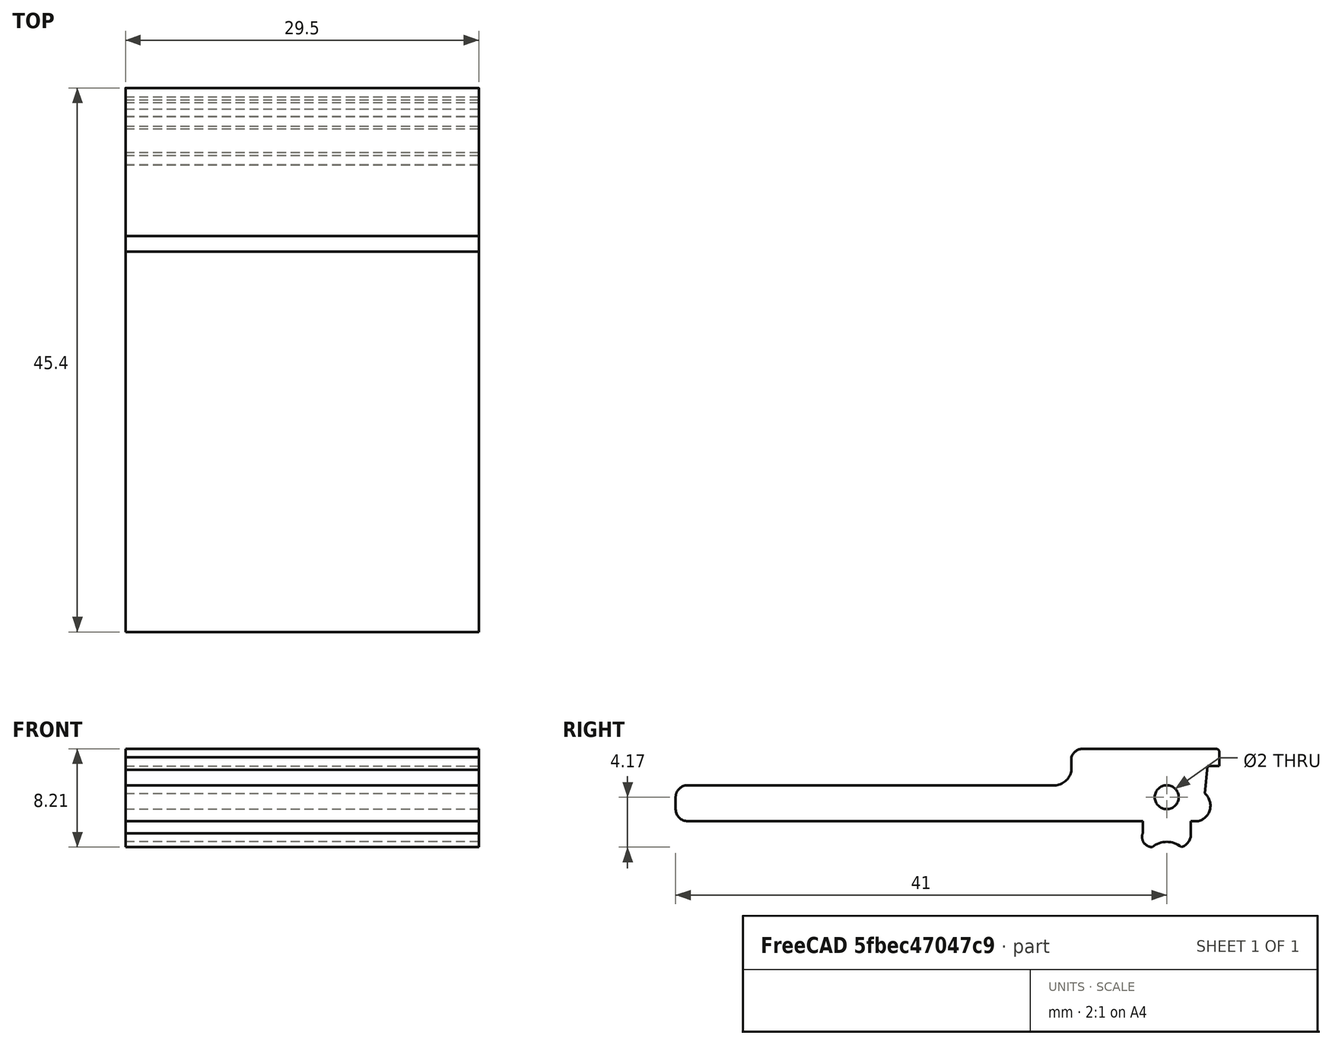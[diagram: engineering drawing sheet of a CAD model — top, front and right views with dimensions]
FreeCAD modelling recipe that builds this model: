
FCSTD DOCUMENT  (FreeCAD 0.19R24267 +99 (Git))
Label: T41 Foot V010
License: All rights reserved
LicenseURL: http://en.wikipedia.org/wiki/All_rights_reserved
objects: Sketcher::SketchObject×1, PartDesign::Pad×1, PartDesign::Body×1
note: 4 computed .brp shape members not serialized (recipe doc carries the construction recipe); baked Part::Feature solids carry a one-line shape summary decoded from their .brp

FEATURE [Sketcher::SketchObject] Sketch
  FullyConstrained = false
  MapMode = 5
  Placement = pos=(0,0,0) rot=(0.57735,0.57735,0.57735;2.0944rad)
  Support = -> [YZ_Plane]
  sketch-geometry (22):
    g0: LineSegment StartX=-41 StartY=9.712e-13 StartZ=0 EndX=-41 EndY=-1 EndZ=0
    g1: LineSegment StartX=-40 StartY=-2 StartZ=0 EndX=-2 EndY=-2 EndZ=0
    g2: ArcOfCircle CenterX=-40 CenterY=9.711e-13 CenterZ=0 NormalX=0 NormalY=0 NormalZ=1 AngleXU=0 Radius=1 StartAngle=1.56519 EndAngle=3.14159
    g3: ArcOfCircle CenterX=-40 CenterY=-1 CenterZ=0 NormalX=0 NormalY=0 NormalZ=1 AngleXU=0 Radius=1 StartAngle=3.14159 EndAngle=4.71239
    g4: LineSegment StartX=4.1 StartY=4.04 StartZ=0 EndX=-7 EndY=4.04 EndZ=0
    g5: ArcOfCircle CenterX=-7 CenterY=3.04 CenterZ=0 NormalX=0 NormalY=0 NormalZ=1 AngleXU=0 Radius=1 StartAngle=1.5708 EndAngle=2.83259
    g6: LineSegment StartX=4.4 StartY=2.59578 StartZ=0 EndX=4.4 EndY=3.74 EndZ=0
    g7: ArcOfCircle CenterX=4.1 CenterY=3.74 CenterZ=0 NormalX=0 NormalY=0 NormalZ=1 AngleXU=0 Radius=0.3 StartAngle=0 EndAngle=1.5708
    g8: Circle CenterX=0 CenterY=0 CenterZ=0 NormalX=0 NormalY=0 NormalZ=1 AngleXU=0 Radius=1
    g9: LineSegment StartX=-39.9944 StartY=0.999984 StartZ=0 EndX=-9.2444 EndY=0.999984 EndZ=0
    g10: ArcOfCircle CenterX=2.3 CenterY=-0.701013 CenterZ=0 NormalX=0 NormalY=0 NormalZ=1 AngleXU=0 Radius=1.34654 StartAngle=4.97895 EndAngle=7.1503
    g11: LineSegment StartX=-7.95264 StartY=3.34411 StartZ=0 EndX=-7.95264 EndY=2.29843 EndZ=0
    g12: ArcOfCircle CenterX=-9.39042 CenterY=2.43704 CenterZ=0 NormalX=0 NormalY=0 NormalZ=1 AngleXU=0 Radius=1.44445 StartAngle=4.81366 EndAngle=6.18708
    g13: LineSegment StartX=2 StartY=-2 StartZ=0 EndX=2 EndY=-3 EndZ=0
    g14: LineSegment StartX=-2 StartY=-3 StartZ=0 EndX=-2 EndY=-2 EndZ=0
    g15: LineSegment StartX=2 StartY=-2 StartZ=0 EndX=2.6547 EndY=-2 EndZ=0
    g16: ArcOfCircle CenterX=0 CenterY=-5.62885 CenterZ=0 NormalX=0 NormalY=0 NormalZ=1 AngleXU=0 Radius=1.9 StartAngle=0.878005 EndAngle=2.26359
    g17: ArcOfCircle CenterX=0.908586 CenterY=-3.11285 CenterZ=0 NormalX=0 NormalY=0 NormalZ=1 AngleXU=0 Radius=1.09723 StartAngle=4.994 EndAngle=6.38622
    g18: ArcOfCircle CenterX=-1.21127 CenterY=-3.31687 CenterZ=0 NormalX=0 NormalY=0 NormalZ=1 AngleXU=0 Radius=0.85 StartAngle=2.75959 EndAngle=4.70976
    g19: LineSegment StartX=3.4 StartY=2.59578 StartZ=0 EndX=4.4 EndY=2.59578 EndZ=0
    g20: LineSegment StartX=3.17125 StartY=0.325684 StartZ=0 EndX=3.4 EndY=2.59578 EndZ=0
    g21: LineSegment StartX=2 StartY=-2 StartZ=0 EndX=2.6547 EndY=-2 EndZ=0
  constraints (53):
    c: Horizontal(g1)
    c: Vertical(g0)
    c: DistanceY(g10,g-1) = 2
    c: Tangent(g0,g2) = -1.5708
    c: Tangent(g1,g3) = -1.5708
    c: Tangent(g0,g3) = -1.5708
    c: Equal(g3,g2)
    c: Radius(g3) = 1
    c: Horizontal(g4)
    c: Tangent(g4,g5) = -1.5708
    c: Vertical(g6)
    c: Tangent(g4,g7) = -1.5708
    c: Tangent(g6,g7) = -1.5708
    c: Radius(g7) = 0.3
    c: Radius(g8) = 1
    c: DistanceX(g8,g-1) = 0
    c: DistanceY(g-1,g8) = 0
    c: Coincident(g9,g2)
    c: Horizontal(g9)
    c: Radius(g5) = 1
    c: DistanceY(g0,g0) = 1
    c: DistanceX(g4,g8) = 7
    c: Coincident(g11,g5)
    c: Vertical(g11)
    c: Coincident(g10,g15)
    c: Coincident(g12,g9)
    c: Vertical(g14)
    c: PointOnObject(g16,g-2)
    c: Radius(g16) = 1.9
    c: DistanceX(g1,g8) = 40
    c: Coincident(g13,g17)
    c: Coincident(g14,g18)
    c: Coincident(g11,g12)
    c: Coincident(g18,g16)
    c: Coincident(g16,g17)
    c: DistanceX(g14,g8) = 2
    c: Coincident(g1,g14)
    c: DistanceX(g8,g13) = 2
    c: Coincident(g13,g15)
    c: DistanceY(g14,g14) = 1
    c: DistanceY(g13,g13) = 1
    c: DistanceX(g9,g9) = 30.75
    c: Radius(g18) = 0.85
    c: Coincident(g20,g19)
    c: Coincident(g19,g6)
    c: Perpendicular(g6,g19)
    c: DistanceY(g8,g4) = 4.04
    c: Horizontal(g16,g16)
    c: Coincident(g10,g20)
    c: DistanceX(g8,g6) = 4.4
    c: Coincident(g10,g13)
    c: Coincident(g21,g13)
    c: Coincident(g21,g10)
FEATURE [PartDesign::Pad] Pad
  Direction = (1,1,1)
  Length = 29.5
  Length2 = 100
  Placement = pos=(0,0,0) rot=(0.57735,0.57735,0.57735;2.0944rad)
  Profile = -> Sketch
  Type = 0
FEATURE [PartDesign::Body] Body
  Group = -> [Sketch,Pad]
  Origin = -> Origin
  Tip = -> Pad
